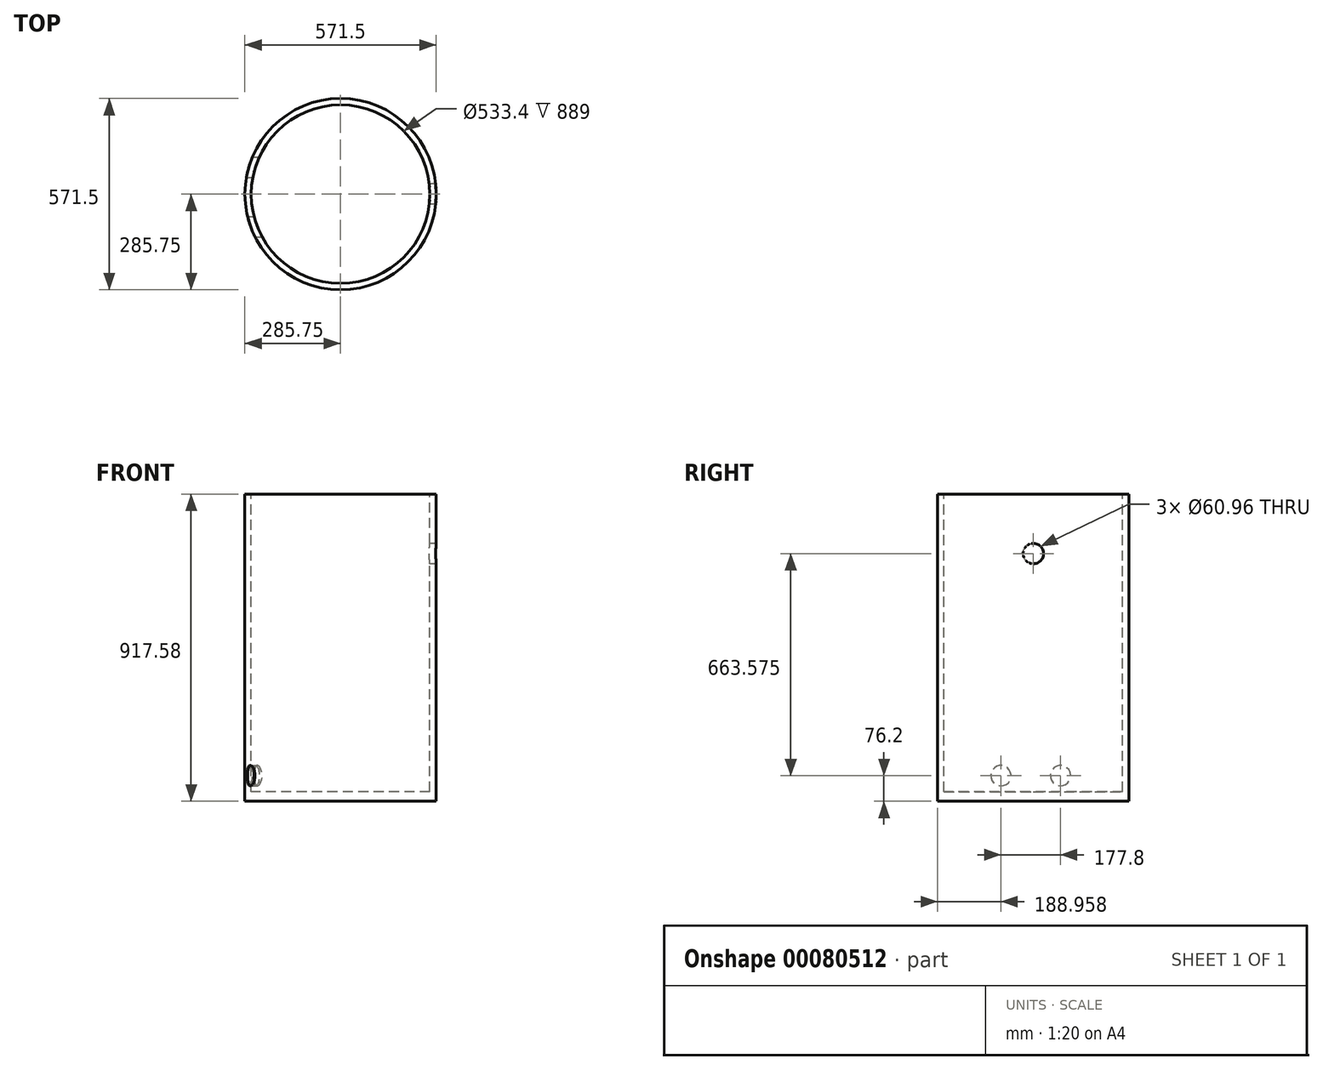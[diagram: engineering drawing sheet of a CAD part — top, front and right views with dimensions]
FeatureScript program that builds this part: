
annotation { "Feature Type Name" : "Feature", "Feature Type Description" : "" }
export const myFeature = defineFeature(function(context is Context, id is Id, definition is map)
    precondition{}
    {
        {
            var Q0;
            Q0=qCreatedBy(makeId("Top.planeOp"),FACE);
            var sketch = newSketch(context, id + "F0", { "sketchPlane" : qUnion([Q0])});
            skCircle(sketch, "E0", {"center": v(0, 0) * mm, "radius": 285.75 * mm});
            skSolve(sketch);
        }
        {
            var Q0;
            Q0=makeQuery(id+"F0.imprint","IMPRINT",FACE,{"disambiguationData":[TD([[makeQuery(id+"F0.imprint","IMPRINT",EDGE,{"derivedFrom":sQuery(id+"F0.wireOp",EDGE,"E0")}),1.0]])]});
            extrude(context, id + "F1", {"entities" : qUnion([Q0]), "depth" : 917.57 * mm});
        }
        {
            var Q0;
            Q0=makeQuery(id+"F1.opExtrude","CAP_FACE",FACE,{"disambiguationData":[OSD([sQuery(id+"F0.wireOp",EDGE,"E0")])],"isStart":false});
            var sketch = newSketch(context, id + "F2", { "sketchPlane" : qUnion([Q0])});
            skCircle(sketch, "E1", {"center": v(0, 0) * mm, "radius": 266.7 * mm});
            skSolve(sketch);
        }
        {
            var Q0;
            Q0=makeQuery(id+"F2.imprint","IMPRINT",FACE,{"disambiguationData":[TD([[makeQuery(id+"F2.imprint","IMPRINT",EDGE,{"derivedFrom":sQuery(id+"F2.wireOp",EDGE,"E1")}),1.0]])]});
            var Q1;
            Q1=sQuery(id+"F2.wireOp",EDGE,"E1");
            extrude(context, id + "F3", {"entities" : qUnion([Q0]), "operationType" : NewBodyOperationType.REMOVE, "surfaceEntities" : qUnion([Q1]), "oppositeDirection" : true, "depth" : 889 * mm});
        }
        {
            var Q0;
            Q0=qCreatedBy(makeId("Right.planeOp"),FACE);
            var sketch = newSketch(context, id + "F4", { "sketchPlane" : qUnion([Q0])});
            skCircle(sketch, "E2", {"center": v(0, 739.78) * mm, "radius": 30.48 * mm});
            skSolve(sketch);
        }
        {
            var Q0;
            Q0 = qSketchRegion(id + "F4", true);
            extrude(context, id + "F5", {"entities" : qUnion([Q0]), "operationType" : NewBodyOperationType.REMOVE, "depth" : 547.83 * mm});
        }
        {
            var Q0;
            Q0=qCreatedBy(makeId("Right.planeOp"),FACE);
            var sketch = newSketch(context, id + "F6", { "sketchPlane" : qUnion([Q0])});
            skCircle(sketch, "E3", {"center": v(81, 76.2) * mm, "radius": 30.48 * mm});
            skCircle(sketch, "E4", {"center": v(-96.8, 76.2) * mm, "radius": 30.48 * mm});
            skSolve(sketch);
        }
        {
            var Q0;
            Q0 = qSketchRegion(id + "F6", true);
            extrude(context, id + "F7", {"entities" : qUnion([Q0]), "operationType" : NewBodyOperationType.REMOVE, "oppositeDirection" : true, "depth" : 651.82 * mm});
        }
    });
